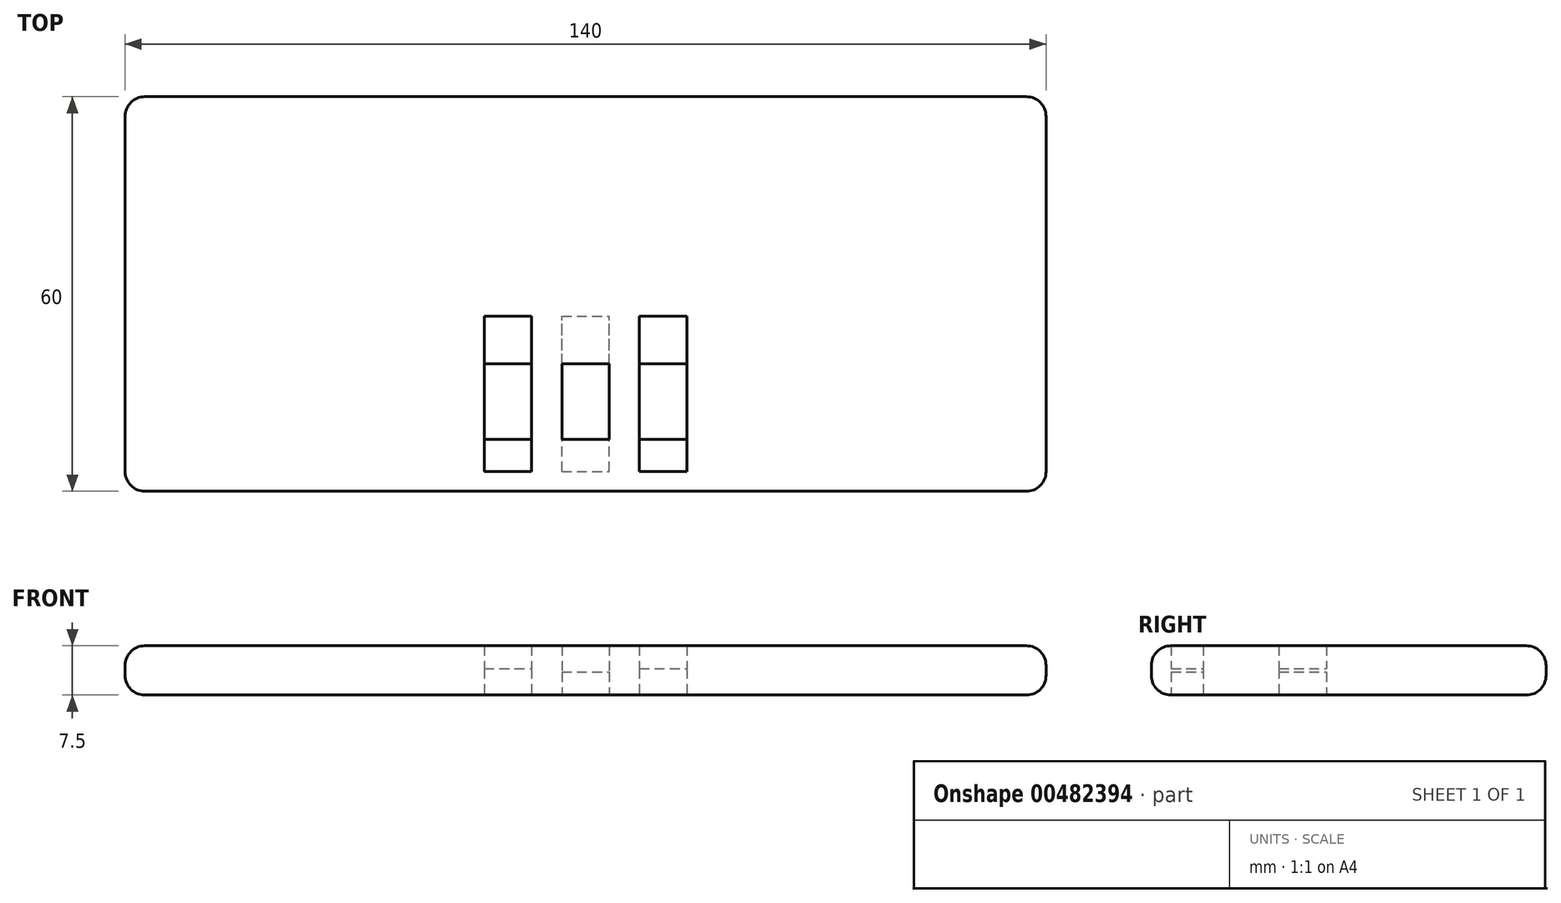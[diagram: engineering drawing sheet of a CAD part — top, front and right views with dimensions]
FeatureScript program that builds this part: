
annotation { "Feature Type Name" : "Feature", "Feature Type Description" : "" }
export const myFeature = defineFeature(function(context is Context, id is Id, definition is map)
    precondition{}
    {
        {
            var Q0;
            Q0=qCreatedBy(makeId("Top.planeOp"),FACE);
            var sketch = newSketch(context, id + "F0", { "sketchPlane" : qUnion([Q0])});
            skLineSegment(sketch, "E0.bottom", {"start": v(70, 30) * mm, "end": v(-70, 30) * mm});
            skLineSegment(sketch, "E0.top", {"start": v(70, -30) * mm, "end": v(-70, -30) * mm});
            skLineSegment(sketch, "E0.left", {"start": v(70, 30) * mm, "end": v(70, -30) * mm});
            skLineSegment(sketch, "E0.right", {"start": v(-70, 30) * mm, "end": v(-70, -30) * mm});
            skPoint(sketch, "E0.middle", {"position": v(0, 0) * mm});
            skSolve(sketch);
        }
        {
            var Q0;
            Q0=qSketchRegion(id+"F0",true);
            extrude(context, id + "F1", {"entities" : qUnion([Q0]), "depth" : 7.5 * mm});
        }
        {
            var Q0;
            Q0=makeQuery(id+"F1.opExtrude","CAP_EDGE",EDGE,{"disambiguationData":[OSD([sQuery(id+"F0.wireOp",EDGE,"E0.top")])],"isStart":false});
            var Q1;
            Q1=makeQuery(id+"F1.opExtrude","CAP_EDGE",EDGE,{"disambiguationData":[OSD([sQuery(id+"F0.wireOp",EDGE,"E0.left")])],"isStart":false});
            var Q2;
            Q2=makeQuery(id+"F1.opExtrude","CAP_EDGE",EDGE,{"disambiguationData":[OSD([sQuery(id+"F0.wireOp",EDGE,"E0.bottom")])],"isStart":false});
            var Q3;
            Q3=makeQuery(id+"F1.opExtrude","CAP_EDGE",EDGE,{"disambiguationData":[OSD([sQuery(id+"F0.wireOp",EDGE,"E0.right")])],"isStart":false});
            var Q4;
            Q4=makeQuery(id+"F1.opExtrude","CAP_EDGE",EDGE,{"disambiguationData":[OSD([sQuery(id+"F0.wireOp",EDGE,"E0.bottom")])],"isStart":true});
            var Q5;
            Q5=makeQuery(id+"F1.opExtrude","SWEPT_EDGE",EDGE,{"disambiguationData":[OSD([sQuery(id+"F0.wireOp",EDGE,"E0.bottom"),sQuery(id+"F0.wireOp",EDGE,"E0.left")])]});
            var Q6;
            Q6=makeQuery(id+"F1.opExtrude","CAP_EDGE",EDGE,{"disambiguationData":[OSD([sQuery(id+"F0.wireOp",EDGE,"E0.left")])],"isStart":true});
            var Q7;
            Q7=makeQuery(id+"F1.opExtrude","SWEPT_EDGE",EDGE,{"disambiguationData":[OSD([sQuery(id+"F0.wireOp",EDGE,"E0.top"),sQuery(id+"F0.wireOp",EDGE,"E0.left")])]});
            var Q8;
            Q8=makeQuery(id+"F1.opExtrude","SWEPT_EDGE",EDGE,{"disambiguationData":[OSD([sQuery(id+"F0.wireOp",EDGE,"E0.bottom"),sQuery(id+"F0.wireOp",EDGE,"E0.right")])]});
            var Q9;
            Q9=makeQuery(id+"F1.opExtrude","CAP_EDGE",EDGE,{"disambiguationData":[OSD([sQuery(id+"F0.wireOp",EDGE,"E0.right")])],"isStart":true});
            var Q10;
            Q10=makeQuery(id+"F1.opExtrude","CAP_EDGE",EDGE,{"disambiguationData":[OSD([sQuery(id+"F0.wireOp",EDGE,"E0.top")])],"isStart":true});
            var Q11;
            Q11=makeQuery(id+"F1.opExtrude","SWEPT_FACE",FACE,{"disambiguationData":[OSD([sQuery(id+"F0.wireOp",EDGE,"E0.top")])]});
            var Q12;
            Q12=makeQuery(id+"F1.opExtrude","SWEPT_EDGE",EDGE,{"disambiguationData":[OSD([sQuery(id+"F0.wireOp",EDGE,"E0.top"),sQuery(id+"F0.wireOp",EDGE,"E0.right")])]});
            fillet(context, id + "F2", {"entities" : qUnion([Q0, Q1, Q2, Q3, Q4, Q5, Q6, Q7, Q8, Q9, Q10, Q11, Q12]), "radius" : 3 * mm, "tangentPropagation" : true, "allowEdgeOverflow" : false});
        }
        {
            var Q0;
            Q0=qCreatedBy(makeId("Top.planeOp"),FACE);
            var sketch = newSketch(context, id + "F3", { "sketchPlane" : qUnion([Q0])});
            skLineSegment(sketch, "E1.bottom", {"start": v(-3.6, -27) * mm, "end": v(3.6, -27) * mm});
            skLineSegment(sketch, "E1.top", {"start": v(-3.6, -3.4) * mm, "end": v(3.6, -3.4) * mm});
            skLineSegment(sketch, "E1.left", {"start": v(-3.6, -27) * mm, "end": v(-3.6, -3.4) * mm});
            skLineSegment(sketch, "E1.right", {"start": v(3.6, -27) * mm, "end": v(3.6, -3.4) * mm});
            skLineSegment(sketch, "E2.bottom", {"start": v(-3.6, -22.1) * mm, "end": v(3.6, -22.1) * mm});
            skLineSegment(sketch, "E2.top", {"start": v(-3.6, -10.6) * mm, "end": v(3.6, -10.6) * mm});
            skLineSegment(sketch, "E2.left", {"start": v(-3.6, -22.1) * mm, "end": v(-3.6, -10.6) * mm});
            skLineSegment(sketch, "E2.right", {"start": v(3.6, -22.1) * mm, "end": v(3.6, -10.6) * mm});
            skLineSegment(sketch, "E3.bottom", {"start": v(-15.4, -27) * mm, "end": v(-8.2, -27) * mm});
            skLineSegment(sketch, "E3.top", {"start": v(-15.4, -3.4) * mm, "end": v(-8.2, -3.4) * mm});
            skLineSegment(sketch, "E3.left", {"start": v(-15.4, -27) * mm, "end": v(-15.4, -3.4) * mm});
            skLineSegment(sketch, "E3.right", {"start": v(-8.2, -27) * mm, "end": v(-8.2, -3.4) * mm});
            skLineSegment(sketch, "E4.bottom", {"start": v(-15.4, -22.1) * mm, "end": v(-8.2, -22.1) * mm});
            skLineSegment(sketch, "E4.top", {"start": v(-15.4, -10.6) * mm, "end": v(-8.2, -10.6) * mm});
            skLineSegment(sketch, "E4.left", {"start": v(-15.4, -22.1) * mm, "end": v(-15.4, -10.6) * mm});
            skLineSegment(sketch, "E4.right", {"start": v(-8.2, -22.1) * mm, "end": v(-8.2, -10.6) * mm});
            skLineSegment(sketch, "E5.bottom", {"start": v(8.2, -27) * mm, "end": v(15.4, -27) * mm});
            skLineSegment(sketch, "E5.top", {"start": v(8.2, -3.4) * mm, "end": v(15.4, -3.4) * mm});
            skLineSegment(sketch, "E5.left", {"start": v(8.2, -27) * mm, "end": v(8.2, -3.4) * mm});
            skLineSegment(sketch, "E5.right", {"start": v(15.4, -27) * mm, "end": v(15.4, -3.4) * mm});
            skLineSegment(sketch, "E6.bottom", {"start": v(8.2, -22.1) * mm, "end": v(15.4, -22.1) * mm});
            skLineSegment(sketch, "E6.top", {"start": v(8.2, -10.6) * mm, "end": v(15.4, -10.6) * mm});
            skLineSegment(sketch, "E6.left", {"start": v(8.2, -22.1) * mm, "end": v(8.2, -10.6) * mm});
            skLineSegment(sketch, "E6.right", {"start": v(15.4, -22.1) * mm, "end": v(15.4, -10.6) * mm});
            skSolve(sketch);
        }
        {
            var Q0;
            {var subQ0=sQuery(id+"F3.wireOp",EDGE,"E1.top");Q0=makeQuery(id+"F3.imprint","IMPRINT",FACE,{"disambiguationData":[TD([[makeQuery(id+"F3.imprint","IMPRINT",EDGE,{"derivedFrom":subQ0}),-1.0]])]});}
            var Q1;
            {var subQ0=sQuery(id+"F3.wireOp",EDGE,"E1.bottom");Q1=makeQuery(id+"F3.imprint","IMPRINT",FACE,{"disambiguationData":[TD([[makeQuery(id+"F3.imprint","IMPRINT",EDGE,{"derivedFrom":subQ0}),1.0]])]});}
            extrude(context, id + "F4", {"entities" : qUnion([Q0, Q1]), "operationType" : NewBodyOperationType.REMOVE, "depth" : 3.5 * mm});
        }
        {
            var Q0;
            Q0=makeQuery(id+"F3.imprint","IMPRINT",FACE,{"disambiguationData":[TD([[makeQuery(id+"F3.imprint","IMPRINT",EDGE,{"derivedFrom":sQuery(id+"F3.wireOp",EDGE,"E2.bottom")}),1.0]])]});
            extrude(context, id + "F5", {"entities" : qUnion([Q0]), "operationType" : NewBodyOperationType.REMOVE, "oppositeDirection" : true, "depth" : -10 * mm});
        }
        {
            var Q0;
            Q0=makeQuery(id+"F3.imprint","IMPRINT",FACE,{"disambiguationData":[TD([[makeQuery(id+"F3.imprint","IMPRINT",EDGE,{"derivedFrom":sQuery(id+"F3.wireOp",EDGE,"E4.bottom")}),1.0]])]});
            var Q1;
            Q1=makeQuery(id+"F3.imprint","IMPRINT",FACE,{"disambiguationData":[TD([[makeQuery(id+"F3.imprint","IMPRINT",EDGE,{"derivedFrom":sQuery(id+"F3.wireOp",EDGE,"E6.bottom")}),1.0]])]});
            extrude(context, id + "F6", {"entities" : qUnion([Q0, Q1]), "operationType" : NewBodyOperationType.REMOVE, "depth" : 25 * mm});
        }
        {
            var Q0;
            {var subQ0=sQuery(id+"F3.wireOp",EDGE,"E3.bottom");Q0=makeQuery(id+"F3.imprint","IMPRINT",FACE,{"disambiguationData":[TD([[makeQuery(id+"F3.imprint","IMPRINT",EDGE,{"derivedFrom":subQ0}),1.0]])]});}
            var Q1;
            {var subQ0=sQuery(id+"F3.wireOp",EDGE,"E3.top");Q1=makeQuery(id+"F3.imprint","IMPRINT",FACE,{"disambiguationData":[TD([[makeQuery(id+"F3.imprint","IMPRINT",EDGE,{"derivedFrom":subQ0}),-1.0]])]});}
            var Q2;
            {var subQ0=sQuery(id+"F3.wireOp",EDGE,"E5.top");Q2=makeQuery(id+"F3.imprint","IMPRINT",FACE,{"disambiguationData":[TD([[makeQuery(id+"F3.imprint","IMPRINT",EDGE,{"derivedFrom":subQ0}),-1.0]])]});}
            var Q3;
            {var subQ0=sQuery(id+"F3.wireOp",EDGE,"E5.bottom");Q3=makeQuery(id+"F3.imprint","IMPRINT",FACE,{"disambiguationData":[TD([[makeQuery(id+"F3.imprint","IMPRINT",EDGE,{"derivedFrom":subQ0}),1.0]])]});}
            extrude(context, id + "F7", {"entities" : qUnion([Q0, Q1, Q2, Q3]), "operationType" : NewBodyOperationType.REMOVE, "depth" : 10 * mm, "hasSecondDirection" : true, "secondDirectionOppositeDirection" : false, "secondDirectionDepth" : 4 * mm});
        }
    });
